# Revit family: Bernhardt_Design-Chair-Lounge-Canelle
name_source: partatom
category: Furniture
revit_build: Autodesk Revit 2016 (Build: 20150714_1515(x64)
units: mm (PartAtom-declared; Revit-internal decimal feet)

## family parameters
Always vertical = Yes
Cut with Voids When Loaded = No
Room Calculation Point = No
Shared = Yes

## types (8) — shared parameters
Manufacturer = Bernhardt Design
Model = Canelle
URL = https://www.bernhardtdesign.com

## per-type parameters (varying)
| type | Metal Base | Pillow Visibility | SKU | Wood Base | Wood Base Material |
| Canell 4756 | Yes | No | Canelle 4756 | No |  |
| Canelle 4756K | Yes | No | Canelle 4756K | No |  |
| Canell 4756P | Yes | Yes | Canelle 4756P | No |  |
| Canell 4756PK | Yes | Yes | Canelle 4756PK | No |  |
| Canelle 4757M | No | No | Canelle 4757M | Yes | <By Category> |
| Canelle 4757PM | No | Yes | Canelle 4757PM | Yes | <By Category> |
| Canelle 4757W | No | No | Canelle 4757W | Yes | <By Category> |
| Canelle 4757PW | No | Yes | Canelle 4757PW | Yes | <By Category> |

## geometry (parser evidence)
native form markers: Blend x4, Sweep x5
no freeform markers — native parametric forms only
